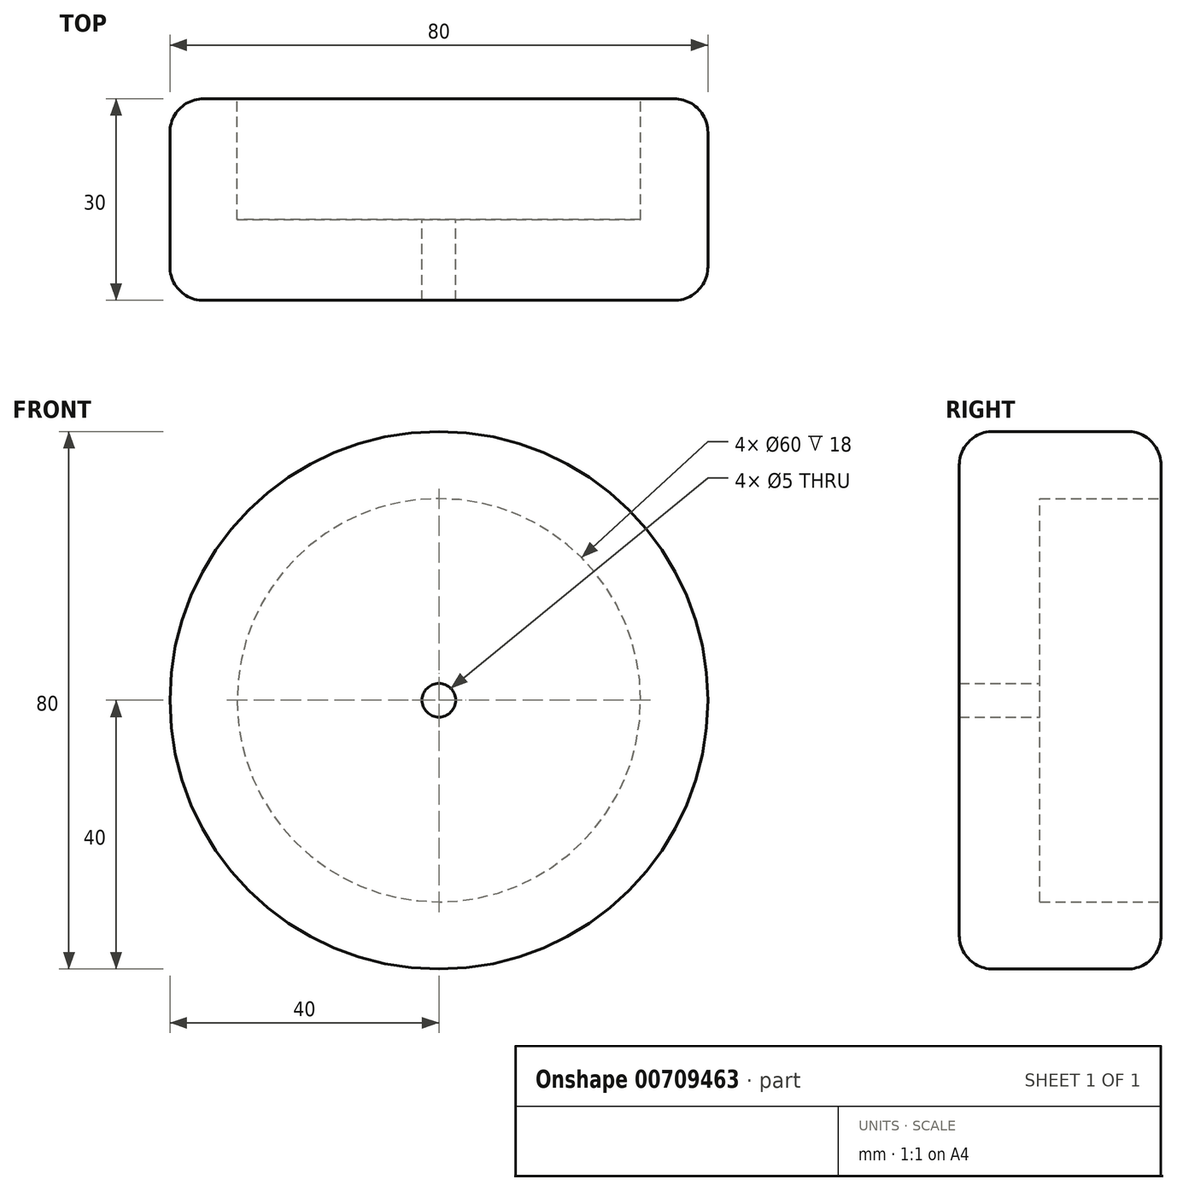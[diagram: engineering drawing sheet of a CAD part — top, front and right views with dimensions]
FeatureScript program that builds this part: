
annotation { "Feature Type Name" : "Feature", "Feature Type Description" : "" }
export const myFeature = defineFeature(function(context is Context, id is Id, definition is map)
    precondition{}
    {
        {
            var Q0;
            Q0=qCreatedBy(makeId("Front.planeOp"),FACE);
            var sketch = newSketch(context, id + "F0", { "sketchPlane" : qUnion([Q0])});
            skCircle(sketch, "E0", {"center": v(0, 0) * mm, "radius": 40 * mm});
            skSolve(sketch);
        }
        {
            var Q0;
            Q0 = qSketchRegion(id + "F0", true);
            extrude(context, id + "F1", {"entities" : qUnion([Q0]), "depth" : 30 * mm, "offsetDistance" : 25 * mm});
        }
        {
            var Q0;
            Q0=makeQuery(id+"F1.opExtrude","SWEPT_FACE",FACE,{"disambiguationData":[OSD([sQuery(id+"F0.wireOp",EDGE,"E0")])]});
            fillet(context, id + "F2", {"entities" : qUnion([Q0]), "radius" : 5 * mm, "tangentPropagation" : true, "allowEdgeOverflow" : false});
        }
        {
            var Q0;
            Q0=qCreatedBy(makeId("Front.planeOp"),FACE);
            var sketch = newSketch(context, id + "F3", { "sketchPlane" : qUnion([Q0])});
            skCircle(sketch, "E1", {"center": v(0, 0) * mm, "radius": 30 * mm});
            skSolve(sketch);
        }
        {
            var Q0;
            Q0 = qSketchRegion(id + "F3", true);
            extrude(context, id + "F4", {"entities" : qUnion([Q0]), "operationType" : NewBodyOperationType.REMOVE, "depth" : 18 * mm, "offsetDistance" : 25 * mm});
        }
        {
            var Q0;
            Q0=qCreatedBy(makeId("Front.planeOp"),FACE);
            var sketch = newSketch(context, id + "F5", { "sketchPlane" : qUnion([Q0])});
            skCircle(sketch, "E2", {"center": v(0, 0) * mm, "radius": 2.5 * mm});
            skSolve(sketch);
        }
        {
            var Q0;
            Q0 = qSketchRegion(id + "F5", true);
            extrude(context, id + "F6", {"entities" : qUnion([Q0]), "operationType" : NewBodyOperationType.REMOVE, "depth" : 41.9 * mm, "offsetDistance" : 25 * mm});
        }
    });
